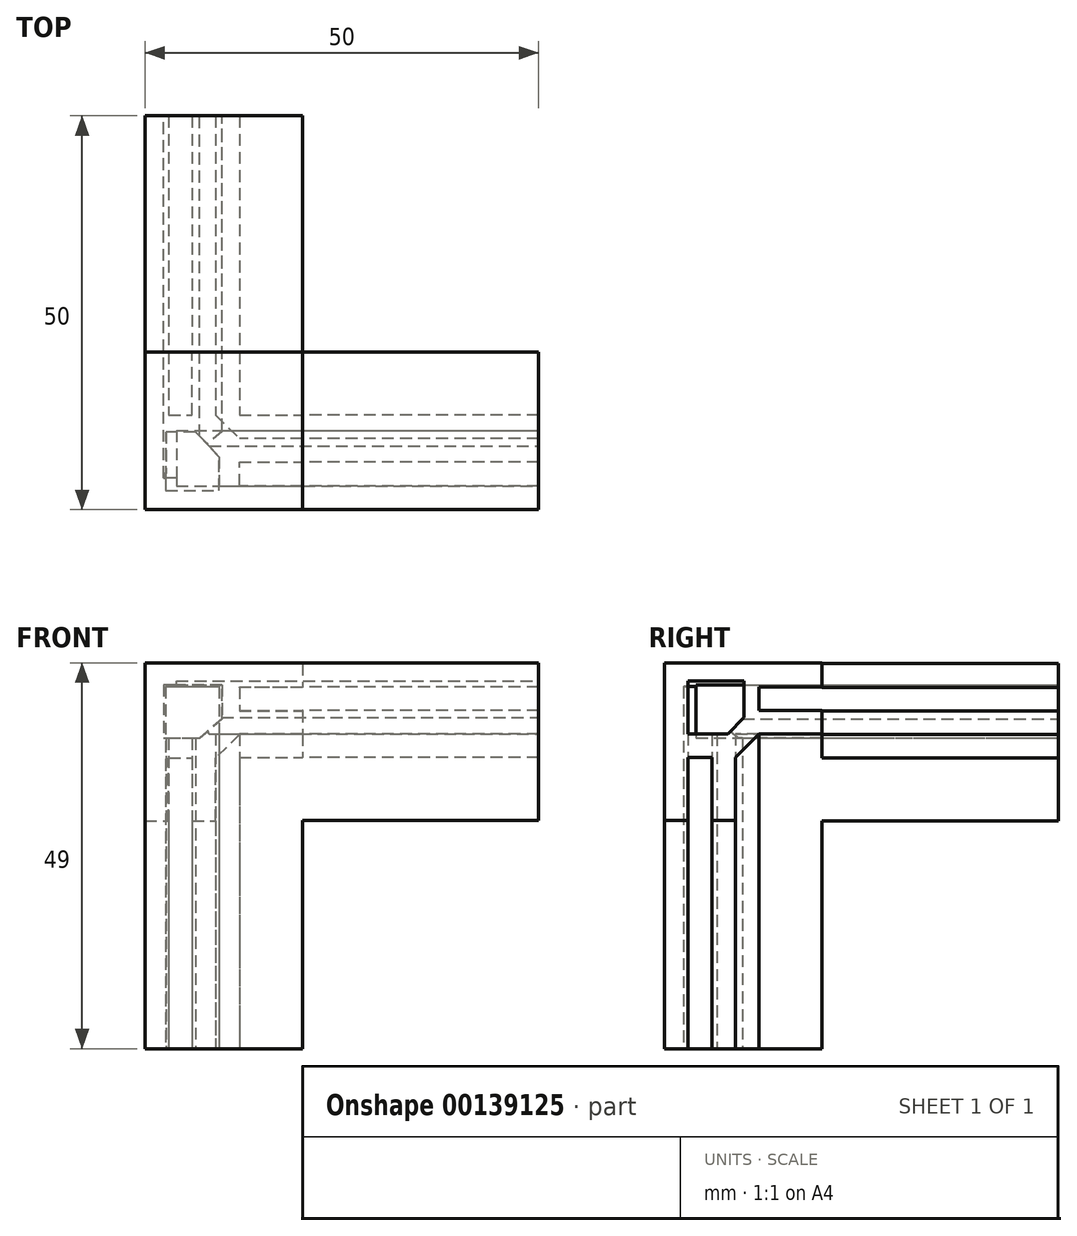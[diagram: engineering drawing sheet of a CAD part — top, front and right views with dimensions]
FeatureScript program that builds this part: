
annotation { "Feature Type Name" : "Feature", "Feature Type Description" : "" }
export const myFeature = defineFeature(function(context is Context, id is Id, definition is map)
    precondition{}
    {
        {
            var Q0;
            Q0=qCreatedBy(makeId("Top.planeOp"),FACE);
            var sketch = newSketch(context, id + "F0", { "sketchPlane" : qUnion([Q0])});
            skLineSegment(sketch, "E0", {"start": v(0, 20) * mm, "end": v(0, 0) * mm});
            skLineSegment(sketch, "E1", {"start": v(0, 0) * mm, "end": v(20, 0) * mm});
            skLineSegment(sketch, "E2", {"start": v(0, 20) * mm, "end": v(3, 20) * mm});
            skLineSegment(sketch, "E3", {"start": v(3, 20) * mm, "end": v(3, 12) * mm});
            skLineSegment(sketch, "E4", {"start": v(3, 12) * mm, "end": v(6, 12) * mm});
            skLineSegment(sketch, "E5", {"start": v(6, 12) * mm, "end": v(6, 20) * mm});
            skLineSegment(sketch, "E6", {"start": v(20, 0) * mm, "end": v(20, 3) * mm});
            skLineSegment(sketch, "E7", {"start": v(20, 3) * mm, "end": v(12, 3) * mm});
            skLineSegment(sketch, "E8", {"start": v(12, 6) * mm, "end": v(20, 6) * mm});
            skLineSegment(sketch, "E9", {"start": v(12, 6) * mm, "end": v(12, 3) * mm});
            skLineSegment(sketch, "E10", {"start": v(20, 6) * mm, "end": v(20, 9) * mm});
            skLineSegment(sketch, "E11", {"start": v(6, 20) * mm, "end": v(9, 20) * mm});
            skLineSegment(sketch, "E12", {"start": v(9, 20) * mm, "end": v(9, 12) * mm});
            skLineSegment(sketch, "E13", {"start": v(20, 9) * mm, "end": v(12, 9) * mm});
            skLineSegment(sketch, "E14", {"start": v(9, 12) * mm, "end": v(12, 9) * mm});
            skSolve(sketch);
        }
        {
            var Q0;
            Q0 = qSketchRegion(id + "F0", true);
            extrude(context, id + "F1", {"entities" : qUnion([Q0]), "depth" : 40 * mm});
        }
        {
            var Q0;
            Q0=makeQuery(id+"F1.opExtrude","CAP_FACE",FACE,{"disambiguationData":[OSD([sQuery(id+"F0.wireOp",EDGE,"E0"),sQuery(id+"F0.wireOp",EDGE,"E1"),sQuery(id+"F0.wireOp",EDGE,"E2"),sQuery(id+"F0.wireOp",EDGE,"E3"),sQuery(id+"F0.wireOp",EDGE,"E4"),sQuery(id+"F0.wireOp",EDGE,"E5"),sQuery(id+"F0.wireOp",EDGE,"E6"),sQuery(id+"F0.wireOp",EDGE,"E7"),sQuery(id+"F0.wireOp",EDGE,"E8"),sQuery(id+"F0.wireOp",EDGE,"E9"),sQuery(id+"F0.wireOp",EDGE,"E10"),sQuery(id+"F0.wireOp",EDGE,"E11"),sQuery(id+"F0.wireOp",EDGE,"E12"),sQuery(id+"F0.wireOp",EDGE,"E13"),sQuery(id+"F0.wireOp",EDGE,"E14")])],"isStart":false});
            cPlane(context, id + "F2", {"entities" : qUnion([Q0]), "cplaneType" : CPlaneType.OFFSET, "offset" : 0 * mm, "width" : 150 * mm, "height" : 150 * mm});
        }
        {
            var Q0;
            Q0=qCreatedBy(id+"F2.planeOp",FACE);
            var sketch = newSketch(context, id + "F3", { "sketchPlane" : qUnion([Q0])});
            skLineSegment(sketch, "E15.bottom", {"start": v(0, 0) * mm, "end": v(20, 0) * mm});
            skLineSegment(sketch, "E15.top", {"start": v(0, 20) * mm, "end": v(20, 20) * mm});
            skLineSegment(sketch, "E15.left", {"start": v(0, 0) * mm, "end": v(0, 20) * mm});
            skLineSegment(sketch, "E15.right", {"start": v(20, 0) * mm, "end": v(20, 20) * mm});
            skSolve(sketch);
        }
        {
            var Q0;
            Q0=makeQuery(id+"F1.opExtrude","SWEPT_FACE",FACE,{"disambiguationData":[OSD([sQuery(id+"F0.wireOp",EDGE,"E6")])]});
            cPlane(context, id + "F4", {"entities" : qUnion([Q0]), "cplaneType" : CPlaneType.OFFSET, "offset" : 0 * mm, "width" : 150 * mm, "height" : 150 * mm});
        }
        {
            var Q0;
            Q0 = qSketchRegion(id + "F3", true);
            extrude(context, id + "F5", {"entities" : qUnion([Q0]), "operationType" : NewBodyOperationType.ADD, "depth" : 9 * mm});
        }
        {
            var Q0;
            Q0=qCreatedBy(id+"F4.planeOp",FACE);
            var sketch = newSketch(context, id + "F6", { "sketchPlane" : qUnion([Q0])});
            skLineSegment(sketch, "E16", {"start": v(0, 48.98) * mm, "end": v(0, 28.98) * mm});
            skLineSegment(sketch, "E17", {"start": v(0, 48.98) * mm, "end": v(20, 48.98) * mm});
            skLineSegment(sketch, "E18", {"start": v(0, 28.98) * mm, "end": v(3, 28.98) * mm});
            skLineSegment(sketch, "E19", {"start": v(3, 28.98) * mm, "end": v(3, 36.98) * mm});
            skLineSegment(sketch, "E20", {"start": v(20, 48.98) * mm, "end": v(20, 45.98) * mm});
            skLineSegment(sketch, "E21", {"start": v(20, 45.98) * mm, "end": v(12, 45.98) * mm});
            skLineSegment(sketch, "E22", {"start": v(12, 45.98) * mm, "end": v(12, 42.98) * mm});
            skLineSegment(sketch, "E23", {"start": v(12, 42.98) * mm, "end": v(20.02, 42.98) * mm});
            skLineSegment(sketch, "E24", {"start": v(20.02, 42.98) * mm, "end": v(20.02, 39.98) * mm});
            skLineSegment(sketch, "E25", {"start": v(20.02, 39.98) * mm, "end": v(12.02, 39.98) * mm});
            skLineSegment(sketch, "E26", {"start": v(3, 36.98) * mm, "end": v(6, 36.98) * mm});
            skLineSegment(sketch, "E27", {"start": v(6, 36.98) * mm, "end": v(6, 28.98) * mm});
            skLineSegment(sketch, "E28", {"start": v(6, 28.98) * mm, "end": v(9, 28.98) * mm});
            skLineSegment(sketch, "E29", {"start": v(9, 28.98) * mm, "end": v(9, 36.98) * mm});
            skLineSegment(sketch, "E30", {"start": v(9, 36.98) * mm, "end": v(12.02, 39.98) * mm});
            skSolve(sketch);
        }
        {
            var Q0;
            Q0=qCreatedBy(id+"F4.planeOp",FACE);
            var sketch = newSketch(context, id + "F7", { "sketchPlane" : qUnion([Q0])});
            skLineSegment(sketch, "E31", {"start": v(20, 45.96) * mm, "end": v(12, 45.96) * mm});
            skLineSegment(sketch, "E32", {"start": v(12, 45.96) * mm, "end": v(12, 42.96) * mm});
            skLineSegment(sketch, "E33", {"start": v(12, 42.96) * mm, "end": v(20, 42.96) * mm});
            skLineSegment(sketch, "E34", {"start": v(20, 42.96) * mm, "end": v(20, 45.96) * mm});
            skLineSegment(sketch, "E35", {"start": v(2.96, 40) * mm, "end": v(2.96, 37) * mm});
            skLineSegment(sketch, "E36", {"start": v(2.96, 37) * mm, "end": v(5.96, 37) * mm});
            skLineSegment(sketch, "E37", {"start": v(5.96, 37) * mm, "end": v(5.96, 40) * mm});
            skLineSegment(sketch, "E38", {"start": v(5.96, 40) * mm, "end": v(2.96, 40) * mm});
            skSolve(sketch);
        }
        {
            var Q0;
            Q0 = qSketchRegion(id + "F7", true);
            extrude(context, id + "F8", {"entities" : qUnion([Q0]), "operationType" : NewBodyOperationType.REMOVE, "oppositeDirection" : true, "depth" : 8 * mm});
        }
        {
            var Q0;
            Q0 = qSketchRegion(id + "F6", true);
            extrude(context, id + "F9", {"entities" : qUnion([Q0]), "operationType" : NewBodyOperationType.ADD, "depth" : 30 * mm});
        }
        {
            var Q0;
            Q0=makeQuery(id+"F9.boolean.opBoolean","MERGE",FACE,{"derivedFrom":[makeQuery(id+"F5.boolean.opBoolean","MERGE",FACE,{"derivedFrom":[makeQuery(id+"F1.opExtrude","SWEPT_FACE",FACE,{"disambiguationData":[OSD([sQuery(id+"F0.wireOp",EDGE,"E2")])]}),makeQuery(id+"F1.opExtrude","SWEPT_FACE",FACE,{"disambiguationData":[OSD([sQuery(id+"F0.wireOp",EDGE,"E11")])]}),makeQuery(id+"F5.opExtrude","SWEPT_FACE",FACE,{"disambiguationData":[OSD([sQuery(id+"F3.wireOp",EDGE,"E15.top")])]})]}),makeQuery(id+"F9.opExtrude","SWEPT_FACE",FACE,{"disambiguationData":[OSD([sQuery(id+"F6.wireOp",EDGE,"E20")])]})]});
            cPlane(context, id + "F10", {"entities" : qUnion([Q0]), "cplaneType" : CPlaneType.OFFSET, "offset" : 0 * mm, "width" : 150 * mm, "height" : 150 * mm});
        }
        {
            var Q0;
            Q0=qCreatedBy(id+"F10.planeOp",FACE);
            var sketch = newSketch(context, id + "F11", { "sketchPlane" : qUnion([Q0])});
            skLineSegment(sketch, "E39", {"start": v(0, 48.91) * mm, "end": v(-20, 48.91) * mm});
            skLineSegment(sketch, "E40", {"start": v(-20, 48.91) * mm, "end": v(-20, 45.91) * mm});
            skLineSegment(sketch, "E41", {"start": v(-20, 45.91) * mm, "end": v(-12, 45.91) * mm});
            skLineSegment(sketch, "E42", {"start": v(-12, 45.91) * mm, "end": v(-12, 42.91) * mm});
            skLineSegment(sketch, "E43", {"start": v(-12, 42.91) * mm, "end": v(-20, 42.91) * mm});
            skLineSegment(sketch, "E44", {"start": v(-20, 42.91) * mm, "end": v(-20, 39.91) * mm});
            skLineSegment(sketch, "E45", {"start": v(-20, 39.91) * mm, "end": v(-12, 39.91) * mm});
            skLineSegment(sketch, "E46", {"start": v(0, 48.91) * mm, "end": v(0, 28.91) * mm});
            skLineSegment(sketch, "E47", {"start": v(0, 28.91) * mm, "end": v(-3, 28.91) * mm});
            skLineSegment(sketch, "E48", {"start": v(-3, 28.91) * mm, "end": v(-3, 36.91) * mm});
            skLineSegment(sketch, "E49", {"start": v(-3, 36.91) * mm, "end": v(-6, 36.91) * mm});
            skLineSegment(sketch, "E50", {"start": v(-6, 36.91) * mm, "end": v(-6, 28.91) * mm});
            skLineSegment(sketch, "E51", {"start": v(-6, 28.91) * mm, "end": v(-9, 28.91) * mm});
            skLineSegment(sketch, "E52", {"start": v(-9, 28.91) * mm, "end": v(-9, 36.91) * mm});
            skLineSegment(sketch, "E53", {"start": v(-12, 39.91) * mm, "end": v(-9, 36.91) * mm});
            skSolve(sketch);
        }
        {
            var Q0;
            Q0 = qSketchRegion(id + "F11", true);
            extrude(context, id + "F12", {"entities" : qUnion([Q0]), "operationType" : NewBodyOperationType.ADD, "depth" : 30 * mm});
        }
        {
            var Q0;
            Q0=makeQuery(id+"F12.opExtrude","CAP_FACE",FACE,{"disambiguationData":[OSD([sQuery(id+"F11.wireOp",EDGE,"E39"),sQuery(id+"F11.wireOp",EDGE,"E40"),sQuery(id+"F11.wireOp",EDGE,"E41"),sQuery(id+"F11.wireOp",EDGE,"E42"),sQuery(id+"F11.wireOp",EDGE,"E43"),sQuery(id+"F11.wireOp",EDGE,"E44"),sQuery(id+"F11.wireOp",EDGE,"E45"),sQuery(id+"F11.wireOp",EDGE,"E46"),sQuery(id+"F11.wireOp",EDGE,"E47"),sQuery(id+"F11.wireOp",EDGE,"E48"),sQuery(id+"F11.wireOp",EDGE,"E49"),sQuery(id+"F11.wireOp",EDGE,"E50"),sQuery(id+"F11.wireOp",EDGE,"E51"),sQuery(id+"F11.wireOp",EDGE,"E52"),sQuery(id+"F11.wireOp",EDGE,"E53")])],"isStart":false});
            cPlane(context, id + "F13", {"entities" : qUnion([Q0]), "cplaneType" : CPlaneType.OFFSET, "offset" : 0 * mm, "width" : 150 * mm, "height" : 150 * mm});
        }
        {
            var Q0;
            Q0=qCreatedBy(id+"F13.planeOp",FACE);
            var sketch = newSketch(context, id + "F14", { "sketchPlane" : qUnion([Q0])});
            skLineSegment(sketch, "E54", {"start": v(-2.39, 39.47) * mm, "end": v(-6.94, 39.47) * mm});
            skLineSegment(sketch, "E55", {"start": v(-6.94, 39.47) * mm, "end": v(-9.78, 41.89) * mm});
            skLineSegment(sketch, "E56", {"start": v(-9.78, 41.89) * mm, "end": v(-9.78, 46.22) * mm});
            skLineSegment(sketch, "E57", {"start": v(-9.78, 46.22) * mm, "end": v(-2.39, 46.22) * mm});
            skLineSegment(sketch, "E58", {"start": v(-2.39, 46.22) * mm, "end": v(-2.39, 39.47) * mm});
            skSolve(sketch);
        }
        {
            var Q0;
            Q0 = qSketchRegion(id + "F14", true);
            extrude(context, id + "F15", {"entities" : qUnion([Q0]), "operationType" : NewBodyOperationType.REMOVE, "oppositeDirection" : true, "depth" : 46 * mm});
        }
        {
            var Q0;
            Q0=makeQuery(id+"F1.opExtrude","CAP_FACE",FACE,{"disambiguationData":[OSD([sQuery(id+"F0.wireOp",EDGE,"E0"),sQuery(id+"F0.wireOp",EDGE,"E1"),sQuery(id+"F0.wireOp",EDGE,"E2"),sQuery(id+"F0.wireOp",EDGE,"E3"),sQuery(id+"F0.wireOp",EDGE,"E4"),sQuery(id+"F0.wireOp",EDGE,"E5"),sQuery(id+"F0.wireOp",EDGE,"E6"),sQuery(id+"F0.wireOp",EDGE,"E7"),sQuery(id+"F0.wireOp",EDGE,"E8"),sQuery(id+"F0.wireOp",EDGE,"E9"),sQuery(id+"F0.wireOp",EDGE,"E10"),sQuery(id+"F0.wireOp",EDGE,"E11"),sQuery(id+"F0.wireOp",EDGE,"E12"),sQuery(id+"F0.wireOp",EDGE,"E13"),sQuery(id+"F0.wireOp",EDGE,"E14")])],"isStart":true});
            cPlane(context, id + "F16", {"entities" : qUnion([Q0]), "cplaneType" : CPlaneType.OFFSET, "offset" : 0 * mm, "width" : 150 * mm, "height" : 150 * mm});
        }
        {
            var Q0;
            Q0=qCreatedBy(id+"F16.planeOp",FACE);
            var sketch = newSketch(context, id + "F17", { "sketchPlane" : qUnion([Q0])});
            skLineSegment(sketch, "E59", {"start": v(2.63, -2.43) * mm, "end": v(9.44, -2.43) * mm});
            skLineSegment(sketch, "E60", {"start": v(9.44, -2.43) * mm, "end": v(9.44, -6.67) * mm});
            skLineSegment(sketch, "E61", {"start": v(9.44, -6.67) * mm, "end": v(6.43, -9.86) * mm});
            skLineSegment(sketch, "E62", {"start": v(6.43, -9.86) * mm, "end": v(2.7, -9.86) * mm});
            skLineSegment(sketch, "E63", {"start": v(2.7, -9.86) * mm, "end": v(2.63, -2.43) * mm});
            skSolve(sketch);
        }
        {
            var Q0;
            Q0 = qSketchRegion(id + "F17", true);
            extrude(context, id + "F18", {"entities" : qUnion([Q0]), "operationType" : NewBodyOperationType.REMOVE, "oppositeDirection" : true, "depth" : 46 * mm});
        }
        {
            var Q0;
            Q0=makeQuery(id+"F9.opExtrude","CAP_FACE",FACE,{"disambiguationData":[OSD([sQuery(id+"F6.wireOp",EDGE,"E16"),sQuery(id+"F6.wireOp",EDGE,"E17"),sQuery(id+"F6.wireOp",EDGE,"E18"),sQuery(id+"F6.wireOp",EDGE,"E19"),sQuery(id+"F6.wireOp",EDGE,"E20"),sQuery(id+"F6.wireOp",EDGE,"E21"),sQuery(id+"F6.wireOp",EDGE,"E22"),sQuery(id+"F6.wireOp",EDGE,"E23"),sQuery(id+"F6.wireOp",EDGE,"E24"),sQuery(id+"F6.wireOp",EDGE,"E25"),sQuery(id+"F6.wireOp",EDGE,"E26"),sQuery(id+"F6.wireOp",EDGE,"E27"),sQuery(id+"F6.wireOp",EDGE,"E28"),sQuery(id+"F6.wireOp",EDGE,"E29"),sQuery(id+"F6.wireOp",EDGE,"E30")])],"isStart":false});
            var sketch = newSketch(context, id + "F19", { "sketchPlane" : qUnion([Q0])});
            skLineSegment(sketch, "E64", {"start": v(3, 39.98) * mm, "end": v(8.05, 39.98) * mm});
            skLineSegment(sketch, "E65", {"start": v(8.05, 39.98) * mm, "end": v(10.05, 42.05) * mm});
            skLineSegment(sketch, "E66", {"start": v(10.05, 42.05) * mm, "end": v(10.05, 46.73) * mm});
            skLineSegment(sketch, "E67", {"start": v(10.05, 46.73) * mm, "end": v(3, 46.73) * mm});
            skLineSegment(sketch, "E68", {"start": v(3, 39.98) * mm, "end": v(3, 46.73) * mm});
            skSolve(sketch);
        }
        {
            var Q0;
            Q0 = qSketchRegion(id + "F19", true);
            extrude(context, id + "F20", {"entities" : qUnion([Q0]), "operationType" : NewBodyOperationType.REMOVE, "oppositeDirection" : true, "depth" : 46 * mm});
        }
    });
